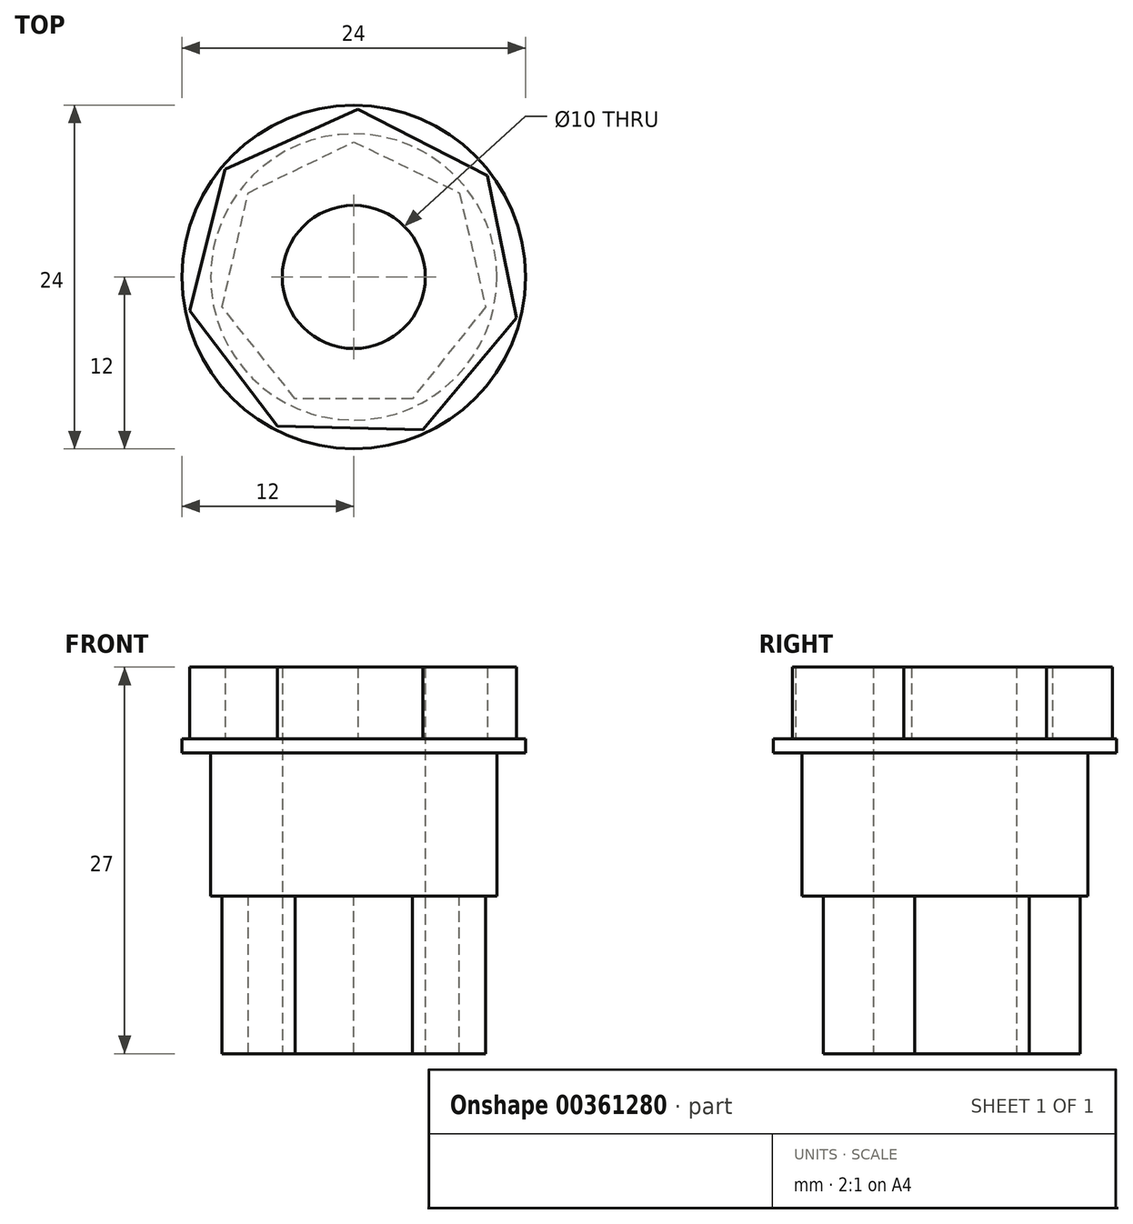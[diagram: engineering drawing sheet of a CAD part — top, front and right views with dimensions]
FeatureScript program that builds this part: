
annotation { "Feature Type Name" : "Feature", "Feature Type Description" : "" }
export const myFeature = defineFeature(function(context is Context, id is Id, definition is map)
    precondition{}
    {
        {
            var Q0;
            Q0=qCreatedBy(makeId("Top.planeOp"),FACE);
            var sketch = newSketch(context, id + "F0", { "sketchPlane" : qUnion([Q0])});
            skPoint(sketch, "E0.center", {"position": v(0, 0) * mm});
            skCircle(sketch, "E1", {"center": v(0, 0) * mm, "radius": 5 * mm});
            skCircle(sketch, "E2", {"center": v(0, 0) * mm, "radius": 10 * mm});
            skCircle(sketch, "E3.cCircle", {"center": v(0, 0) * mm, "radius": 10.55 * mm, "construction": true});
            skLineSegment(sketch, "E3.0", {"start": v(11.35, -2.87) * mm, "end": v(4.84, -10.66) * mm});
            skLineSegment(sketch, "E3.1", {"start": v(4.84, -10.66) * mm, "end": v(-5.32, -10.43) * mm});
            skLineSegment(sketch, "E3.2", {"start": v(-5.32, -10.43) * mm, "end": v(-11.47, -2.34) * mm});
            skLineSegment(sketch, "E3.3", {"start": v(-11.47, -2.34) * mm, "end": v(-8.98, 7.5) * mm});
            skLineSegment(sketch, "E3.4", {"start": v(-8.98, 7.5) * mm, "end": v(0.27, 11.7) * mm});
            skLineSegment(sketch, "E3.5", {"start": v(0.27, 11.7) * mm, "end": v(9.32, 7.09) * mm});
            skLineSegment(sketch, "E3.6", {"start": v(9.32, 7.09) * mm, "end": v(11.35, -2.87) * mm});
            skPoint(sketch, "E3.0.midPoint", {"position": v(8.1, -6.77) * mm});
            skCircle(sketch, "E4", {"center": v(0, 0) * mm, "radius": 12 * mm});
            skCircle(sketch, "E5.cCircle", {"center": v(0, 0) * mm, "radius": 8.5 * mm, "construction": true});
            skLineSegment(sketch, "E5.0", {"start": v(4.1, -8.5) * mm, "end": v(-4.1, -8.5) * mm});
            skLineSegment(sketch, "E5.1", {"start": v(-4.1, -8.5) * mm, "end": v(-9.2, -2.1) * mm});
            skLineSegment(sketch, "E5.2", {"start": v(-9.2, -2.1) * mm, "end": v(-7.38, 5.88) * mm});
            skLineSegment(sketch, "E5.3", {"start": v(-7.38, 5.88) * mm, "end": v(0, 9.43) * mm});
            skLineSegment(sketch, "E5.4", {"start": v(0, 9.43) * mm, "end": v(7.38, 5.88) * mm});
            skLineSegment(sketch, "E5.5", {"start": v(7.38, 5.88) * mm, "end": v(9.2, -2.1) * mm});
            skLineSegment(sketch, "E5.6", {"start": v(9.2, -2.1) * mm, "end": v(4.1, -8.5) * mm});
            skPoint(sketch, "E5.0.midPoint", {"position": v(0, -8.5) * mm});
            skSolve(sketch);
        }
        {
            var Q0;
            Q0=makeQuery(id+"F0.imprint","IMPRINT",FACE,{"disambiguationData":[TD([[makeQuery(id+"F0.imprint","IMPRINT",EDGE,{"derivedFrom":sQuery(id+"F0.wireOp",EDGE,"E1")}),-1.0]])]});
            var Q1;
            Q1=makeQuery(id+"F0.imprint","IMPRINT",FACE,{"disambiguationData":[TD([[makeQuery(id+"F0.imprint","IMPRINT",EDGE,{"derivedFrom":sQuery(id+"F0.wireOp",EDGE,"E2")}),1.0]])]});
            var Q2;
            Q2=makeQuery(id+"F0.imprint","IMPRINT",FACE,{"disambiguationData":[TD([[makeQuery(id+"F0.imprint","IMPRINT",EDGE,{"derivedFrom":sQuery(id+"F0.wireOp",EDGE,"E2")}),-1.0]])]});
            extrude(context, id + "F1", {"entities" : qUnion([Q0, Q1, Q2]), "depth" : 16 * mm});
        }
        {
            var Q0;
            Q0=makeQuery(id+"F0.imprint","IMPRINT",FACE,{"disambiguationData":[TD([[makeQuery(id+"F0.imprint","IMPRINT",EDGE,{"derivedFrom":sQuery(id+"F0.wireOp",EDGE,"E3.0")}),1.0]])]});
            extrude(context, id + "F2", {"entities" : qUnion([Q0]), "operationType" : NewBodyOperationType.ADD, "depth" : 11 * mm});
        }
        {
            var Q0;
            Q0=makeQuery(id+"F0.imprint","IMPRINT",FACE,{"disambiguationData":[TD([[makeQuery(id+"F0.imprint","IMPRINT",EDGE,{"derivedFrom":sQuery(id+"F0.wireOp",EDGE,"E3.0")}),1.0]])]});
            extrude(context, id + "F3", {"entities" : qUnion([Q0]), "operationType" : NewBodyOperationType.REMOVE, "depth" : 10 * mm});
        }
        {
            var Q0;
            Q0=makeQuery(id+"F0.imprint","IMPRINT",FACE,{"disambiguationData":[TD([[makeQuery(id+"F0.imprint","IMPRINT",EDGE,{"derivedFrom":sQuery(id+"F0.wireOp",EDGE,"E2")}),-1.0]])]});
            extrude(context, id + "F4", {"entities" : qUnion([Q0]), "operationType" : NewBodyOperationType.REMOVE, "depth" : 10 * mm});
        }
        {
            var Q0;
            Q0=makeQuery(id+"F0.imprint","IMPRINT",FACE,{"disambiguationData":[TD([[makeQuery(id+"F0.imprint","IMPRINT",EDGE,{"derivedFrom":sQuery(id+"F0.wireOp",EDGE,"E1")}),-1.0]])]});
            extrude(context, id + "F5", {"entities" : qUnion([Q0]), "operationType" : NewBodyOperationType.ADD, "oppositeDirection" : true, "depth" : 11 * mm});
        }
    });
